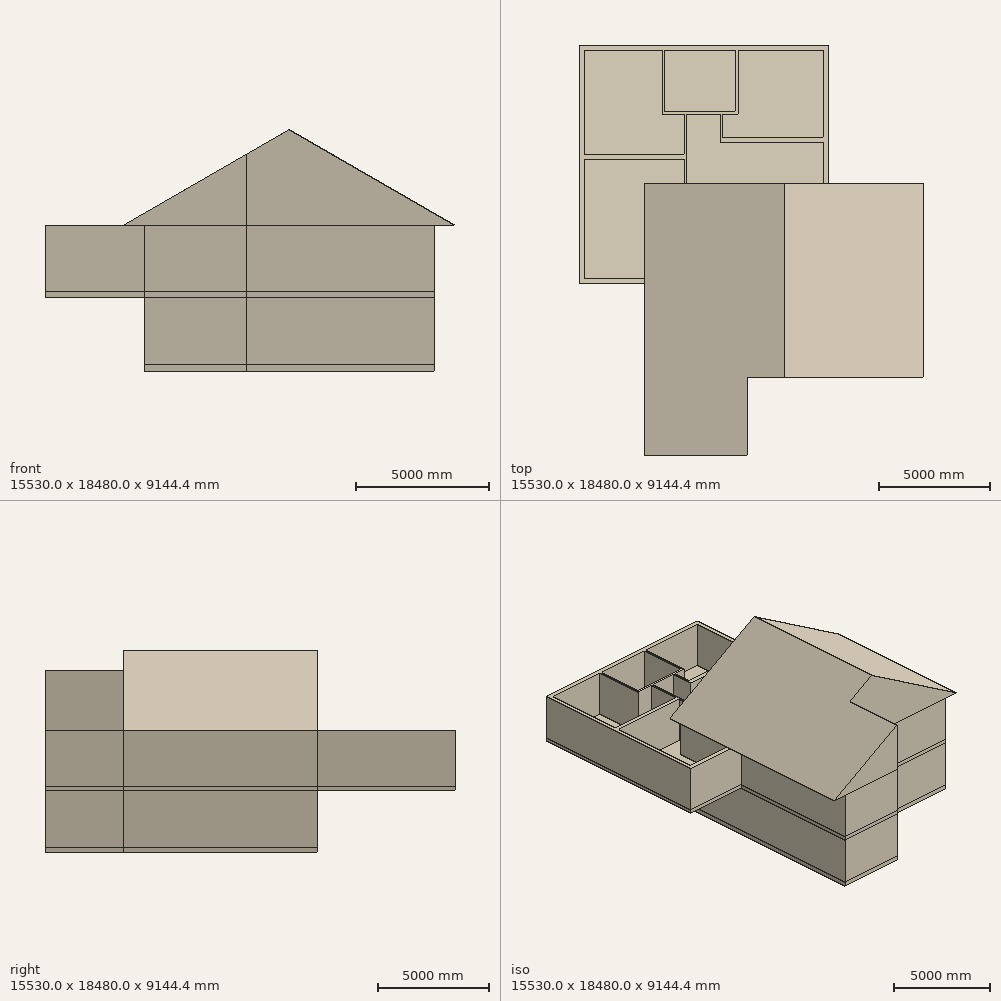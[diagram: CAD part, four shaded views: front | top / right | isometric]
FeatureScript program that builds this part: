
annotation { "Feature Type Name" : "Feature", "Feature Type Description" : "" }
export const myFeature = defineFeature(function(context is Context, id is Id, definition is map)
    precondition{}
    {
        {
            var Q0;
            Q0=qCreatedBy(makeId("Top.planeOp"),FACE);
            var sketch = newSketch(context, id + "F0", { "sketchPlane" : qUnion([Q0])});
            skLineSegment(sketch, "E0.bottom", {"start": v(5495, 4370) * mm, "end": v(-5495, 4370) * mm});
            skLineSegment(sketch, "E0.left", {"start": v(5495, 4370) * mm, "end": v(5495, -4370) * mm});
            skLineSegment(sketch, "E0.right", {"start": v(-5495, 4370) * mm, "end": v(-5495, -4370) * mm});
            skPoint(sketch, "E0.middle", {"position": v(0, 0) * mm});
            skLineSegment(sketch, "E1.top", {"start": v(-5495, -7870) * mm, "end": v(-1630, -7870) * mm});
            skLineSegment(sketch, "E1.left", {"start": v(-5495, -4370) * mm, "end": v(-5495, -7870) * mm});
            skLineSegment(sketch, "E1.right", {"start": v(-1630, -4370) * mm, "end": v(-1630, -7870) * mm});
            skLineSegment(sketch, "E2", {"start": v(-1630, -4370) * mm, "end": v(5495, -4370) * mm});
            skLineSegment(sketch, "E3", {"start": v(-5255, 4070) * mm, "end": v(-5255, -7630) * mm});
            skLineSegment(sketch, "E4", {"start": v(-5255, -7630) * mm, "end": v(-1870, -7630) * mm});
            skLineSegment(sketch, "E5", {"start": v(-1870, -7630) * mm, "end": v(-1870, -4130) * mm});
            skLineSegment(sketch, "E6", {"start": v(-1870, -4130) * mm, "end": v(5255, -4130) * mm});
            skLineSegment(sketch, "E7", {"start": v(5255, -4130) * mm, "end": v(5255, 4070) * mm});
            skLineSegment(sketch, "E8", {"start": v(5255, 4070) * mm, "end": v(-5255, 4070) * mm});
            skLineSegment(sketch, "E9", {"start": v(-5255, 120) * mm, "end": v(5255, 120) * mm});
            skLineSegment(sketch, "E10", {"start": v(5255, 120) * mm, "end": v(5255, -120) * mm});
            skLineSegment(sketch, "E11", {"start": v(5255, -120) * mm, "end": v(-5255, -120) * mm});
            skLineSegment(sketch, "E12", {"start": v(-5255, 1937.84) * mm, "end": v(-2735, 1937.84) * mm});
            skLineSegment(sketch, "E13", {"start": v(-2735, 1937.84) * mm, "end": v(-2735, 2177.84) * mm});
            skLineSegment(sketch, "E14", {"start": v(-2735, 2177.84) * mm, "end": v(-5255, 2177.84) * mm});
            skLineSegment(sketch, "E15", {"start": v(-1870, -4130) * mm, "end": v(-1870, -120) * mm});
            skLineSegment(sketch, "E16", {"start": v(-1870, -120) * mm, "end": v(-1630, -120) * mm});
            skLineSegment(sketch, "E17", {"start": v(-1630, -120) * mm, "end": v(-1630, -4130) * mm});
            skLineSegment(sketch, "E18", {"start": v(-5255, -2005) * mm, "end": v(-1870, -2005) * mm});
            skLineSegment(sketch, "E19", {"start": v(-1870, -2005) * mm, "end": v(-1870, -2120) * mm});
            skLineSegment(sketch, "E20", {"start": v(-1870, -2120) * mm, "end": v(-5255, -2120) * mm});
            skLineSegment(sketch, "E21", {"start": v(-5255, -4120) * mm, "end": v(-1870, -4120) * mm});
            skLineSegment(sketch, "E22", {"start": v(-1870, -4120) * mm, "end": v(-1870, -4235) * mm});
            skLineSegment(sketch, "E23", {"start": v(-1870, -4235) * mm, "end": v(-5255, -4235) * mm});
            skLineSegment(sketch, "E24", {"start": v(2120, 4070) * mm, "end": v(2120, 120) * mm});
            skLineSegment(sketch, "E25", {"start": v(2120, 120) * mm, "end": v(2005, 120) * mm});
            skLineSegment(sketch, "E26", {"start": v(2005, 120) * mm, "end": v(2005, 4070) * mm});
            skLineSegment(sketch, "E27", {"start": v(2005, 1620) * mm, "end": v(-1141.55, 1620) * mm});
            skLineSegment(sketch, "E28", {"start": v(-1141.55, 1620) * mm, "end": v(-1141.55, 1735) * mm});
            skLineSegment(sketch, "E29", {"start": v(-1141.55, 1735) * mm, "end": v(2005, 1735) * mm});
            skLineSegment(sketch, "E30.bottom", {"start": v(-1680, 4070) * mm, "end": v(-2130, 4070) * mm});
            skLineSegment(sketch, "E30.top", {"start": v(-1680, 3090) * mm, "end": v(-2130, 3090) * mm});
            skLineSegment(sketch, "E30.left", {"start": v(-1680, 4070) * mm, "end": v(-1680, 3090) * mm});
            skLineSegment(sketch, "E30.right", {"start": v(-2130, 4070) * mm, "end": v(-2130, 3090) * mm});
            skSolve(sketch);
        }
        {
            var Q0;
            Q0=makeQuery(id+"F0.imprint","IMPRINT",FACE,{"disambiguationData":[TD([[makeQuery(id+"F0.imprint","IMPRINT",EDGE,{"derivedFrom":sQuery(id+"F0.wireOp",EDGE,"E0.bottom")}),1.0]])]});
            var Q1;
            {var subQ0=sQuery(id+"F0.wireOp",EDGE,"E12");Q1=makeQuery(id+"F0.imprint","IMPRINT",FACE,{"disambiguationData":[TD([[makeQuery(id+"F0.imprint","IMPRINT",EDGE,{"derivedFrom":subQ0}),1.0]])]});}
            var Q2;
            Q2=makeQuery(id+"F0.imprint","IMPRINT",FACE,{"disambiguationData":[TD([[makeQuery(id+"F0.imprint","IMPRINT",EDGE,{"derivedFrom":sQuery(id+"F0.wireOp",EDGE,"E30.top")}),-1.0]])]});
            var Q3;
            {var subQ5=sQuery(id+"F0.wireOp",EDGE,"E24");Q3=makeQuery(id+"F0.imprint","IMPRINT",FACE,{"disambiguationData":[TD([[makeQuery(id+"F0.imprint","IMPRINT",EDGE,{"derivedFrom":subQ5}),1.0]])]});}
            var Q4;
            {var subQ0=sQuery(id+"F0.wireOp",EDGE,"E17");Q4=makeQuery(id+"F0.imprint","IMPRINT",FACE,{"disambiguationData":[TD([[makeQuery(id+"F0.imprint","IMPRINT",EDGE,{"derivedFrom":subQ0}),1.0]])]});}
            var Q5;
            {var subQ0=sQuery(id+"F0.wireOp",EDGE,"E18");Q5=makeQuery(id+"F0.imprint","IMPRINT",FACE,{"disambiguationData":[TD([[makeQuery(id+"F0.imprint","IMPRINT",EDGE,{"derivedFrom":subQ0}),1.0]])]});}
            var Q6;
            {var subQ0=sQuery(id+"F0.wireOp",EDGE,"E20");Q6=makeQuery(id+"F0.imprint","IMPRINT",FACE,{"disambiguationData":[TD([[makeQuery(id+"F0.imprint","IMPRINT",EDGE,{"derivedFrom":subQ0}),1.0]])]});}
            var Q7;
            {var subQ2=sQuery(id+"F0.wireOp",EDGE,"E4");Q7=makeQuery(id+"F0.imprint","IMPRINT",FACE,{"disambiguationData":[TD([[makeQuery(id+"F0.imprint","IMPRINT",EDGE,{"derivedFrom":subQ2}),1.0]])]});}
            var Q8;
            {var subQ6=sQuery(id+"F0.wireOp",EDGE,"E17");Q8=makeQuery(id+"F0.imprint","IMPRINT",FACE,{"disambiguationData":[TD([[makeQuery(id+"F0.imprint","IMPRINT",EDGE,{"derivedFrom":subQ6}),-1.0]])]});}
            var Q9;
            {var subQ2=sQuery(id+"F0.wireOp",EDGE,"E18");Q9=makeQuery(id+"F0.imprint","IMPRINT",FACE,{"disambiguationData":[TD([[makeQuery(id+"F0.imprint","IMPRINT",EDGE,{"derivedFrom":subQ2}),-1.0]])]});}
            var Q10;
            {var subQ0=sQuery(id+"F0.wireOp",EDGE,"E21");Q10=makeQuery(id+"F0.imprint","IMPRINT",FACE,{"disambiguationData":[TD([[makeQuery(id+"F0.imprint","IMPRINT",EDGE,{"derivedFrom":subQ0}),-1.0]])]});}
            var Q11;
            {var subQ0=sQuery(id+"F0.wireOp",EDGE,"E9");var subQ4=sQuery(id+"F0.wireOp",EDGE,"E3");var subQ5=makeQuery(id+"F0.imprint","INTERSECT",VERTEX,{"derivedFrom":[subQ4,subQ0]});Q11=makeQuery(id+"F0.imprint","IMPRINT",FACE,{"disambiguationData":[TD([[makeQuery(id+"F0.imprint","IMPRINT",EDGE,{"disambiguationData":[TD([[subQ5,-1.0]])],"derivedFrom":subQ4}),1.0]])]});}
            var Q12;
            {var subQ11=sQuery(id+"F0.wireOp",EDGE,"E12");Q12=makeQuery(id+"F0.imprint","IMPRINT",FACE,{"disambiguationData":[TD([[makeQuery(id+"F0.imprint","IMPRINT",EDGE,{"derivedFrom":subQ11}),-1.0]])]});}
            var Q13;
            {var subQ0=sQuery(id+"F0.wireOp",EDGE,"E24");Q13=makeQuery(id+"F0.imprint","IMPRINT",FACE,{"disambiguationData":[TD([[makeQuery(id+"F0.imprint","IMPRINT",EDGE,{"derivedFrom":subQ0}),-1.0]])]});}
            var Q14;
            {var subQ2=sQuery(id+"F0.wireOp",EDGE,"E27");Q14=makeQuery(id+"F0.imprint","IMPRINT",FACE,{"disambiguationData":[TD([[makeQuery(id+"F0.imprint","IMPRINT",EDGE,{"derivedFrom":subQ2}),-1.0]])]});}
            extrude(context, id + "F1", {"entities" : qUnion([Q0, Q1, Q2, Q3, Q4, Q5, Q6, Q7, Q8, Q9, Q10, Q11, Q12, Q13, Q14]), "oppositeDirection" : true, "depth" : 250 * mm, "offsetDistance" : 25 * mm});
        }
        {
            var Q0;
            {var subQ0=sQuery(id+"F0.wireOp",EDGE,"E12");Q0=makeQuery(id+"F0.imprint","IMPRINT",FACE,{"disambiguationData":[TD([[makeQuery(id+"F0.imprint","IMPRINT",EDGE,{"derivedFrom":subQ0}),1.0]])]});}
            var Q1;
            Q1=makeQuery(id+"F0.imprint","IMPRINT",FACE,{"disambiguationData":[TD([[makeQuery(id+"F0.imprint","IMPRINT",EDGE,{"derivedFrom":sQuery(id+"F0.wireOp",EDGE,"E0.bottom")}),1.0]])]});
            var Q2;
            {var subQ0=sQuery(id+"F0.wireOp",EDGE,"E9");var subQ4=sQuery(id+"F0.wireOp",EDGE,"E3");var subQ5=makeQuery(id+"F0.imprint","INTERSECT",VERTEX,{"derivedFrom":[subQ4,subQ0]});Q2=makeQuery(id+"F0.imprint","IMPRINT",FACE,{"disambiguationData":[TD([[makeQuery(id+"F0.imprint","IMPRINT",EDGE,{"disambiguationData":[TD([[subQ5,-1.0]])],"derivedFrom":subQ4}),1.0]])]});}
            var Q3;
            {var subQ6=sQuery(id+"F0.wireOp",EDGE,"E17");Q3=makeQuery(id+"F0.imprint","IMPRINT",FACE,{"disambiguationData":[TD([[makeQuery(id+"F0.imprint","IMPRINT",EDGE,{"derivedFrom":subQ6}),-1.0]])]});}
            var Q4;
            {var subQ0=sQuery(id+"F0.wireOp",EDGE,"E24");Q4=makeQuery(id+"F0.imprint","IMPRINT",FACE,{"disambiguationData":[TD([[makeQuery(id+"F0.imprint","IMPRINT",EDGE,{"derivedFrom":subQ0}),-1.0]])]});}
            var Q5;
            Q5=makeQuery(id+"F0.imprint","IMPRINT",FACE,{"disambiguationData":[TD([[makeQuery(id+"F0.imprint","IMPRINT",EDGE,{"derivedFrom":sQuery(id+"F0.wireOp",EDGE,"E30.top")}),-1.0]])]});
            var Q6;
            {var subQ2=sQuery(id+"F0.wireOp",EDGE,"E27");Q6=makeQuery(id+"F0.imprint","IMPRINT",FACE,{"disambiguationData":[TD([[makeQuery(id+"F0.imprint","IMPRINT",EDGE,{"derivedFrom":subQ2}),-1.0]])]});}
            var Q7;
            {var subQ2=sQuery(id+"F0.wireOp",EDGE,"E18");Q7=makeQuery(id+"F0.imprint","IMPRINT",FACE,{"disambiguationData":[TD([[makeQuery(id+"F0.imprint","IMPRINT",EDGE,{"derivedFrom":subQ2}),-1.0]])]});}
            var Q8;
            {var subQ0=sQuery(id+"F0.wireOp",EDGE,"E21");Q8=makeQuery(id+"F0.imprint","IMPRINT",FACE,{"disambiguationData":[TD([[makeQuery(id+"F0.imprint","IMPRINT",EDGE,{"derivedFrom":subQ0}),-1.0]])]});}
            extrude(context, id + "F2", {"entities" : qUnion([Q0, Q1, Q2, Q3, Q4, Q5, Q6, Q7, Q8]), "depth" : 2560 * mm, "offsetDistance" : 25 * mm});
        }
        {
            var Q0;
            Q0=makeQuery(id+"F2.opExtrude","CAP_FACE",FACE,{"disambiguationData":[OSD([sQuery(id+"F0.wireOp",EDGE,"E0.bottom"),sQuery(id+"F0.wireOp",EDGE,"E0.left"),sQuery(id+"F0.wireOp",EDGE,"E0.right"),sQuery(id+"F0.wireOp",EDGE,"E1.top"),sQuery(id+"F0.wireOp",EDGE,"E1.left"),sQuery(id+"F0.wireOp",EDGE,"E1.right"),sQuery(id+"F0.wireOp",EDGE,"E2"),sQuery(id+"F0.wireOp",EDGE,"E3"),sQuery(id+"F0.wireOp",EDGE,"E4"),sQuery(id+"F0.wireOp",EDGE,"E5"),sQuery(id+"F0.wireOp",EDGE,"E6"),sQuery(id+"F0.wireOp",EDGE,"E7"),sQuery(id+"F0.wireOp",EDGE,"E8"),sQuery(id+"F0.wireOp",EDGE,"E9"),sQuery(id+"F0.wireOp",EDGE,"E11"),sQuery(id+"F0.wireOp",EDGE,"E12"),sQuery(id+"F0.wireOp",EDGE,"E13"),sQuery(id+"F0.wireOp",EDGE,"E14"),sQuery(id+"F0.wireOp",EDGE,"E15"),sQuery(id+"F0.wireOp",EDGE,"E17"),sQuery(id+"F0.wireOp",EDGE,"E18"),sQuery(id+"F0.wireOp",EDGE,"E20"),sQuery(id+"F0.wireOp",EDGE,"E21"),sQuery(id+"F0.wireOp",EDGE,"E23"),sQuery(id+"F0.wireOp",EDGE,"E24"),sQuery(id+"F0.wireOp",EDGE,"E26"),sQuery(id+"F0.wireOp",EDGE,"E27"),sQuery(id+"F0.wireOp",EDGE,"E28"),sQuery(id+"F0.wireOp",EDGE,"E29"),sQuery(id+"F0.wireOp",EDGE,"E30.top"),sQuery(id+"F0.wireOp",EDGE,"E30.left"),sQuery(id+"F0.wireOp",EDGE,"E30.right")])],"isStart":false});
            var sketch = newSketch(context, id + "F3", { "sketchPlane" : qUnion([Q0])});
            skLineSegment(sketch, "E31.bottom", {"start": v(-5495, 4370) * mm, "end": v(5495, 4370) * mm});
            skLineSegment(sketch, "E31.left", {"start": v(-5495, 4370) * mm, "end": v(-5495, -4370) * mm});
            skLineSegment(sketch, "E31.right", {"start": v(5495, 4370) * mm, "end": v(5495, -4370) * mm});
            skLineSegment(sketch, "E32.top", {"start": v(-5495, -7870) * mm, "end": v(-1630, -7870) * mm});
            skLineSegment(sketch, "E32.left", {"start": v(-5495, -4370) * mm, "end": v(-5495, -7870) * mm});
            skLineSegment(sketch, "E32.right", {"start": v(-1630, -4370) * mm, "end": v(-1630, -7870) * mm});
            skLineSegment(sketch, "E33", {"start": v(-1630, -4370) * mm, "end": v(5495, -4370) * mm});
            skLineSegment(sketch, "E34", {"start": v(-5255, 1937.84) * mm, "end": v(-2655, 1937.84) * mm});
            skLineSegment(sketch, "E35", {"start": v(-2655, 1937.84) * mm, "end": v(-2655, 120) * mm});
            skLineSegment(sketch, "E36", {"start": v(-2655, 120) * mm, "end": v(-5255, 120) * mm});
            skLineSegment(sketch, "E37", {"start": v(-5255, 120) * mm, "end": v(-5255, 1937.84) * mm});
            skSolve(sketch);
        }
        {
            var Q0;
            Q0 = qSketchRegion(id + "F3", true);
            extrude(context, id + "F4", {"entities" : qUnion([Q0]), "depth" : 200 * mm, "offsetDistance" : 25 * mm});
        }
        {
            var Q0;
            Q0=makeQuery(id+"F4.opExtrude","CAP_FACE",FACE,{"disambiguationData":[OSD([sQuery(id+"F3.wireOp",EDGE,"E31.bottom"),sQuery(id+"F3.wireOp",EDGE,"E31.left"),sQuery(id+"F3.wireOp",EDGE,"E31.right"),sQuery(id+"F3.wireOp",EDGE,"E32.top"),sQuery(id+"F3.wireOp",EDGE,"E32.left"),sQuery(id+"F3.wireOp",EDGE,"E32.right"),sQuery(id+"F3.wireOp",EDGE,"E33"),sQuery(id+"F3.wireOp",EDGE,"E34"),sQuery(id+"F3.wireOp",EDGE,"E35"),sQuery(id+"F3.wireOp",EDGE,"E36"),sQuery(id+"F3.wireOp",EDGE,"E37")])],"isStart":false});
            var sketch = newSketch(context, id + "F5", { "sketchPlane" : qUnion([Q0])});
            skLineSegment(sketch, "E38.bottom", {"start": v(-5495, 4370) * mm, "end": v(5495, 4370) * mm});
            skLineSegment(sketch, "E38.left", {"start": v(-5495, 4370) * mm, "end": v(-5495, -4370) * mm});
            skLineSegment(sketch, "E38.right", {"start": v(5495, 4370) * mm, "end": v(5495, -4370) * mm});
            skLineSegment(sketch, "E39.top", {"start": v(-5495, -7870) * mm, "end": v(-1630, -7870) * mm});
            skLineSegment(sketch, "E39.left", {"start": v(-5495, -4370) * mm, "end": v(-5495, -7870) * mm});
            skLineSegment(sketch, "E39.right", {"start": v(-1630, -4370) * mm, "end": v(-1630, -7870) * mm});
            skLineSegment(sketch, "E40", {"start": v(-1630, -4370) * mm, "end": v(5495, -4370) * mm});
            skLineSegment(sketch, "E41", {"start": v(-5176.2, 4130) * mm, "end": v(5255, 4130) * mm});
            skLineSegment(sketch, "E42", {"start": v(5255, 4130) * mm, "end": v(5255, -4130) * mm});
            skLineSegment(sketch, "E43", {"start": v(5255, -4130) * mm, "end": v(-1630, -4130) * mm});
            skLineSegment(sketch, "E44", {"start": v(-1630, -4130) * mm, "end": v(-1630, -3530) * mm});
            skLineSegment(sketch, "E45", {"start": v(-1630, -3530) * mm, "end": v(-1870, -3530) * mm});
            skLineSegment(sketch, "E46", {"start": v(-1870, -3530) * mm, "end": v(-1870, -7630) * mm});
            skLineSegment(sketch, "E47", {"start": v(-1870, -7630) * mm, "end": v(-5255, -7630) * mm});
            skLineSegment(sketch, "E48", {"start": v(-5255, -7630) * mm, "end": v(-5255, 3762.1) * mm});
            skLineSegment(sketch, "E49", {"start": v(-5255, 3762.1) * mm, "end": v(-5255, 4130) * mm});
            skLineSegment(sketch, "E50", {"start": v(-5255, 4130) * mm, "end": v(-5176.2, 4130) * mm});
            skLineSegment(sketch, "E51", {"start": v(-5255, 120) * mm, "end": v(-5255, -121.14) * mm});
            skLineSegment(sketch, "E52", {"start": v(-5255, 120) * mm, "end": v(5255, 120) * mm});
            skLineSegment(sketch, "E53", {"start": v(5255, 120) * mm, "end": v(5255, -119.88) * mm});
            skLineSegment(sketch, "E54", {"start": v(-5255, -120) * mm, "end": v(5255, -120) * mm});
            skLineSegment(sketch, "E55.bottom", {"start": v(-1680, 4130) * mm, "end": v(-2128.3, 4130) * mm});
            skLineSegment(sketch, "E55.top", {"start": v(-1680, 3088.74) * mm, "end": v(-2128.3, 3088.74) * mm});
            skLineSegment(sketch, "E55.left", {"start": v(-1680, 4130) * mm, "end": v(-1680, 3088.74) * mm});
            skLineSegment(sketch, "E55.right", {"start": v(-2128.3, 4130) * mm, "end": v(-2128.3, 3088.74) * mm});
            skLineSegment(sketch, "E56", {"start": v(-5255, 1937.84) * mm, "end": v(-1680, 1937.84) * mm});
            skLineSegment(sketch, "E57", {"start": v(-1680, 1937.84) * mm, "end": v(-1680, 2052.84) * mm});
            skLineSegment(sketch, "E58", {"start": v(-1680, 2052.84) * mm, "end": v(-5255, 2052.84) * mm});
            skLineSegment(sketch, "E59", {"start": v(2120, 4130) * mm, "end": v(2120, 120) * mm});
            skLineSegment(sketch, "E60", {"start": v(2120, 120) * mm, "end": v(2005, 120) * mm});
            skLineSegment(sketch, "E61", {"start": v(2005, 120) * mm, "end": v(2005, 4130) * mm});
            skLineSegment(sketch, "E62", {"start": v(130.73, 4130) * mm, "end": v(130.73, 2052.84) * mm});
            skLineSegment(sketch, "E63", {"start": v(130.73, 2052.84) * mm, "end": v(245.73, 2052.84) * mm});
            skLineSegment(sketch, "E64", {"start": v(245.73, 2052.84) * mm, "end": v(245.73, 4130) * mm});
            skLineSegment(sketch, "E65", {"start": v(1995, 4370) * mm, "end": v(1995, 10610) * mm});
            skLineSegment(sketch, "E66", {"start": v(1995, 10610) * mm, "end": v(-9235, 10610) * mm});
            skLineSegment(sketch, "E67", {"start": v(-9235, 10610) * mm, "end": v(-9235, -130) * mm});
            skLineSegment(sketch, "E68", {"start": v(-9235, -130) * mm, "end": v(-5495, -130) * mm});
            skLineSegment(sketch, "E69", {"start": v(-8995, 10370) * mm, "end": v(1755, 10370) * mm});
            skLineSegment(sketch, "E70", {"start": v(1755, 10370) * mm, "end": v(1755, 4370) * mm});
            skLineSegment(sketch, "E71", {"start": v(-8995, 10370) * mm, "end": v(-8995, 110) * mm});
            skLineSegment(sketch, "E72", {"start": v(-8995, 110) * mm, "end": v(-5495, 110) * mm});
            skLineSegment(sketch, "E73", {"start": v(-3829.03, 4370) * mm, "end": v(-3714.03, 4370) * mm});
            skLineSegment(sketch, "E74", {"start": v(-8995, 5710) * mm, "end": v(-4495, 5710) * mm});
            skLineSegment(sketch, "E75", {"start": v(-4495, 5710) * mm, "end": v(-4495, 5470) * mm});
            skLineSegment(sketch, "E76", {"start": v(-4495, 5470) * mm, "end": v(-8995, 5470) * mm});
            skLineSegment(sketch, "E77", {"start": v(1755, 6230) * mm, "end": v(-2765, 6230) * mm});
            skLineSegment(sketch, "E78", {"start": v(-2765, 6230) * mm, "end": v(-2765, 6470) * mm});
            skLineSegment(sketch, "E79", {"start": v(-2765, 6470) * mm, "end": v(1755, 6470) * mm});
            skLineSegment(sketch, "E80", {"start": v(-4495, 4372.22) * mm, "end": v(-4380, 4372.22) * mm});
            skLineSegment(sketch, "E81", {"start": v(-2765, 6230) * mm, "end": v(-2880, 6230) * mm});
            skLineSegment(sketch, "E82", {"start": v(-2880, 6230) * mm, "end": v(-2880, 7516.83) * mm});
            skLineSegment(sketch, "E83", {"start": v(-2880, 7516.83) * mm, "end": v(-4376.77, 7516.83) * mm});
            skLineSegment(sketch, "E84", {"start": v(-4376.77, 7516.83) * mm, "end": v(-4376.77, 7631.83) * mm});
            skLineSegment(sketch, "E85", {"start": v(-4376.77, 7631.83) * mm, "end": v(-2765, 7631.83) * mm});
            skLineSegment(sketch, "E86", {"start": v(-2765, 7631.83) * mm, "end": v(-2765, 6470) * mm});
            skLineSegment(sketch, "E87", {"start": v(-4495, 4372.22) * mm, "end": v(-4495, 7516.83) * mm});
            skLineSegment(sketch, "E88", {"start": v(-4495, 7516.83) * mm, "end": v(-4380, 7516.83) * mm});
            skLineSegment(sketch, "E89", {"start": v(-4380, 7516.83) * mm, "end": v(-4380, 4370) * mm});
            skLineSegment(sketch, "E90", {"start": v(-4495, 7516.83) * mm, "end": v(-5495, 7516.83) * mm});
            skLineSegment(sketch, "E91", {"start": v(-5495, 7516.83) * mm, "end": v(-5495, 10370) * mm});
            skLineSegment(sketch, "E92", {"start": v(-5495, 10370) * mm, "end": v(-5380, 10370) * mm});
            skLineSegment(sketch, "E93", {"start": v(-5380, 10370) * mm, "end": v(-5380, 7631.83) * mm});
            skLineSegment(sketch, "E94", {"start": v(-5380, 7631.83) * mm, "end": v(-4376.77, 7631.83) * mm});
            skLineSegment(sketch, "E95", {"start": v(-2182.89, 10370) * mm, "end": v(-2182.89, 7631.83) * mm});
            skLineSegment(sketch, "E96", {"start": v(-2182.89, 7631.83) * mm, "end": v(-2765, 7631.83) * mm});
            skLineSegment(sketch, "E97", {"start": v(-2067.89, 10370) * mm, "end": v(-2067.89, 7516.83) * mm});
            skLineSegment(sketch, "E98", {"start": v(-2067.89, 7516.83) * mm, "end": v(-2765, 7516.83) * mm});
            skLineSegment(sketch, "E99", {"start": v(-4380, 7516.83) * mm, "end": v(-4376.77, 7516.83) * mm});
            skSolve(sketch);
        }
        {
            var Q0;
            {var subQ10=sQuery(id+"F5.wireOp",EDGE,"E65");Q0=makeQuery(id+"F5.imprint","IMPRINT",FACE,{"disambiguationData":[TD([[makeQuery(id+"F5.imprint","IMPRINT",EDGE,{"derivedFrom":subQ10}),1.0]])]});}
            var Q1;
            {var subQ0=sQuery(id+"F5.wireOp",EDGE,"E74");Q1=makeQuery(id+"F5.imprint","IMPRINT",FACE,{"disambiguationData":[TD([[makeQuery(id+"F5.imprint","IMPRINT",EDGE,{"derivedFrom":subQ0}),1.0]])]});}
            var Q2;
            Q2=makeQuery(id+"F5.imprint","IMPRINT",FACE,{"disambiguationData":[TD([[makeQuery(id+"F5.imprint","IMPRINT",EDGE,{"derivedFrom":sQuery(id+"F5.wireOp",EDGE,"E85")}),1.0]])]});
            var Q3;
            {var subQ3=sQuery(id+"F5.wireOp",EDGE,"E77");Q3=makeQuery(id+"F5.imprint","IMPRINT",FACE,{"disambiguationData":[TD([[makeQuery(id+"F5.imprint","IMPRINT",EDGE,{"derivedFrom":subQ3}),1.0]])]});}
            var Q4;
            {var subQ2=sQuery(id+"F5.wireOp",EDGE,"E72");Q4=makeQuery(id+"F5.imprint","IMPRINT",FACE,{"disambiguationData":[TD([[makeQuery(id+"F5.imprint","IMPRINT",EDGE,{"derivedFrom":subQ2}),1.0]])]});}
            var Q5;
            {var subQ2=sQuery(id+"F5.wireOp",EDGE,"E74");Q5=makeQuery(id+"F5.imprint","IMPRINT",FACE,{"disambiguationData":[TD([[makeQuery(id+"F5.imprint","IMPRINT",EDGE,{"derivedFrom":subQ2}),-1.0]])]});}
            var Q6;
            {var subQ0=sQuery(id+"F5.wireOp",EDGE,"E77");Q6=makeQuery(id+"F5.imprint","IMPRINT",FACE,{"disambiguationData":[TD([[makeQuery(id+"F5.imprint","IMPRINT",EDGE,{"derivedFrom":subQ0}),-1.0]])]});}
            var Q7;
            {var subQ1=sQuery(id+"F5.wireOp",EDGE,"E79");Q7=makeQuery(id+"F5.imprint","IMPRINT",FACE,{"disambiguationData":[TD([[makeQuery(id+"F5.imprint","IMPRINT",EDGE,{"derivedFrom":subQ1}),1.0]])]});}
            var Q8;
            {var subQ5=sQuery(id+"F5.wireOp",EDGE,"E95");Q8=makeQuery(id+"F5.imprint","IMPRINT",FACE,{"disambiguationData":[TD([[makeQuery(id+"F5.imprint","IMPRINT",EDGE,{"derivedFrom":subQ5}),1.0]])]});}
            var Q9;
            {var subQ0=sQuery(id+"F5.wireOp",EDGE,"E78");Q9=makeQuery(id+"F5.imprint","IMPRINT",FACE,{"disambiguationData":[TD([[makeQuery(id+"F5.imprint","IMPRINT",EDGE,{"derivedFrom":subQ0}),1.0]])]});}
            var Q10;
            {var subQ1=sQuery(id+"F5.wireOp",EDGE,"E75");Q10=makeQuery(id+"F5.imprint","IMPRINT",FACE,{"disambiguationData":[TD([[makeQuery(id+"F5.imprint","IMPRINT",EDGE,{"derivedFrom":subQ1}),1.0]])]});}
            extrude(context, id + "F6", {"entities" : qUnion([Q0, Q1, Q2, Q3, Q4, Q5, Q6, Q7, Q8, Q9, Q10]), "oppositeDirection" : true, "depth" : 200 * mm, "offsetDistance" : 25 * mm});
        }
        {
            var Q0;
            {var subQ10=sQuery(id+"F5.wireOp",EDGE,"E65");Q0=makeQuery(id+"F5.imprint","IMPRINT",FACE,{"disambiguationData":[TD([[makeQuery(id+"F5.imprint","IMPRINT",EDGE,{"derivedFrom":subQ10}),1.0]])]});}
            var Q1;
            {var subQ2=sQuery(id+"F5.wireOp",EDGE,"E74");Q1=makeQuery(id+"F5.imprint","IMPRINT",FACE,{"disambiguationData":[TD([[makeQuery(id+"F5.imprint","IMPRINT",EDGE,{"derivedFrom":subQ2}),-1.0]])]});}
            var Q2;
            {var subQ1=sQuery(id+"F5.wireOp",EDGE,"E75");Q2=makeQuery(id+"F5.imprint","IMPRINT",FACE,{"disambiguationData":[TD([[makeQuery(id+"F5.imprint","IMPRINT",EDGE,{"derivedFrom":subQ1}),1.0]])]});}
            var Q3;
            {var subQ0=sQuery(id+"F5.wireOp",EDGE,"E77");Q3=makeQuery(id+"F5.imprint","IMPRINT",FACE,{"disambiguationData":[TD([[makeQuery(id+"F5.imprint","IMPRINT",EDGE,{"derivedFrom":subQ0}),-1.0]])]});}
            var Q4;
            {var subQ5=sQuery(id+"F5.wireOp",EDGE,"E95");Q4=makeQuery(id+"F5.imprint","IMPRINT",FACE,{"disambiguationData":[TD([[makeQuery(id+"F5.imprint","IMPRINT",EDGE,{"derivedFrom":subQ5}),1.0]])]});}
            var Q5;
            {var subQ0=sQuery(id+"F5.wireOp",EDGE,"E78");Q5=makeQuery(id+"F5.imprint","IMPRINT",FACE,{"disambiguationData":[TD([[makeQuery(id+"F5.imprint","IMPRINT",EDGE,{"derivedFrom":subQ0}),1.0]])]});}
            var Q6;
            Q6=makeQuery(id+"F5.imprint","IMPRINT",FACE,{"disambiguationData":[TD([[makeQuery(id+"F5.imprint","IMPRINT",EDGE,{"derivedFrom":sQuery(id+"F5.wireOp",EDGE,"E84")}),1.0]])]});
            extrude(context, id + "F7", {"entities" : qUnion([Q0, Q1, Q2, Q3, Q4, Q5, Q6]), "depth" : 2500 * mm, "offsetDistance" : 25 * mm});
        }
        {
            var Q0;
            {var subQ19=sQuery(id+"F5.wireOp",EDGE,"E38.right");Q0=makeQuery(id+"F5.imprint","IMPRINT",FACE,{"disambiguationData":[TD([[makeQuery(id+"F5.imprint","IMPRINT",EDGE,{"derivedFrom":subQ19}),-1.0]])]});}
            var Q1;
            {var subQ0=sQuery(id+"F5.wireOp",EDGE,"E54");Q1=makeQuery(id+"F5.imprint","IMPRINT",FACE,{"disambiguationData":[TD([[makeQuery(id+"F5.imprint","IMPRINT",EDGE,{"derivedFrom":subQ0}),1.0]])]});}
            var Q2;
            {var subQ0=sQuery(id+"F5.wireOp",EDGE,"E59");Q2=makeQuery(id+"F5.imprint","IMPRINT",FACE,{"disambiguationData":[TD([[makeQuery(id+"F5.imprint","IMPRINT",EDGE,{"derivedFrom":subQ0}),-1.0]])]});}
            var Q3;
            Q3=makeQuery(id+"F5.imprint","IMPRINT",FACE,{"disambiguationData":[TD([[makeQuery(id+"F5.imprint","IMPRINT",EDGE,{"derivedFrom":sQuery(id+"F5.wireOp",EDGE,"E55.top")}),-1.0]])]});
            var Q4;
            {var subQ0=sQuery(id+"F5.wireOp",EDGE,"E57");Q4=makeQuery(id+"F5.imprint","IMPRINT",FACE,{"disambiguationData":[TD([[makeQuery(id+"F5.imprint","IMPRINT",EDGE,{"derivedFrom":subQ0}),1.0]])]});}
            var Q5;
            {var subQ2=sQuery(id+"F5.wireOp",EDGE,"E62");Q5=makeQuery(id+"F5.imprint","IMPRINT",FACE,{"disambiguationData":[TD([[makeQuery(id+"F5.imprint","IMPRINT",EDGE,{"derivedFrom":subQ2}),1.0]])]});}
            extrude(context, id + "F8", {"entities" : qUnion([Q0, Q1, Q2, Q3, Q4, Q5]), "depth" : 2500 * mm, "offsetDistance" : 25 * mm});
        }
        {
            var Q0;
            Q0=makeQuery(id+"F8.opExtrude","SWEPT_FACE",FACE,{"disambiguationData":[OSD([sQuery(id+"F5.wireOp",EDGE,"E39.top")])]});
            var sketch = newSketch(context, id + "F9", { "sketchPlane" : qUnion([Q0])});
            skLineSegment(sketch, "E100", {"start": v(-1870, 5260) * mm, "end": v(-1870, 9974.06) * mm});
            skLineSegment(sketch, "E101", {"start": v(-1870, 9974.06) * mm, "end": v(6295, 5260) * mm});
            skLineSegment(sketch, "E102", {"start": v(6295, 5260) * mm, "end": v(-10035, 5260) * mm});
            skLineSegment(sketch, "E103", {"start": v(-10035, 5260) * mm, "end": v(-1870, 9974.06) * mm});
            skLineSegment(sketch, "E104", {"start": v(0, 8894.42) * mm, "end": v(-6295, 5260) * mm});
            skLineSegment(sketch, "E105", {"start": v(-1630, 5260) * mm, "end": v(-1630, 7953.34) * mm});
            skSolve(sketch);
        }
        {
            var Q0;
            {var subQ0=sQuery(id+"F9.wireOp",EDGE,"E102");var subQ1=sQuery(id+"F9.wireOp",EDGE,"E100");var subQ2=makeQuery(id+"F9.imprint","INTERSECT",VERTEX,{"derivedFrom":[subQ1,subQ0]});Q0=makeQuery(id+"F9.imprint","IMPRINT",FACE,{"disambiguationData":[TD([[makeQuery(id+"F9.imprint","IMPRINT",EDGE,{"disambiguationData":[TD([[subQ2,-1.0]])],"derivedFrom":subQ1}),1.0]])]});}
            var Q1;
            {var subQ5=sQuery(id+"F9.wireOp",EDGE,"E105");Q1=makeQuery(id+"F9.imprint","IMPRINT",FACE,{"disambiguationData":[TD([[makeQuery(id+"F9.imprint","IMPRINT",EDGE,{"derivedFrom":subQ5}),1.0]])]});}
            var Q2;
            {var subQ5=sQuery(id+"F9.wireOp",EDGE,"E105");Q2=makeQuery(id+"F9.imprint","IMPRINT",FACE,{"disambiguationData":[TD([[makeQuery(id+"F9.imprint","IMPRINT",EDGE,{"derivedFrom":subQ5}),-1.0]])]});}
            extrude(context, id + "F10", {"entities" : qUnion([Q0, Q1, Q2]), "oppositeDirection" : true, "depth" : 12240 * mm, "offsetDistance" : 25 * mm});
        }
        {
            var Q0;
            {var subQ5=sQuery(id+"F9.wireOp",EDGE,"E105");Q0=makeQuery(id+"F9.imprint","IMPRINT",FACE,{"disambiguationData":[TD([[makeQuery(id+"F9.imprint","IMPRINT",EDGE,{"derivedFrom":subQ5}),-1.0]])]});}
            extrude(context, id + "F11", {"entities" : qUnion([Q0]), "operationType" : NewBodyOperationType.REMOVE, "oppositeDirection" : true, "depth" : 3500 * mm, "offsetDistance" : 25 * mm});
        }
    });
